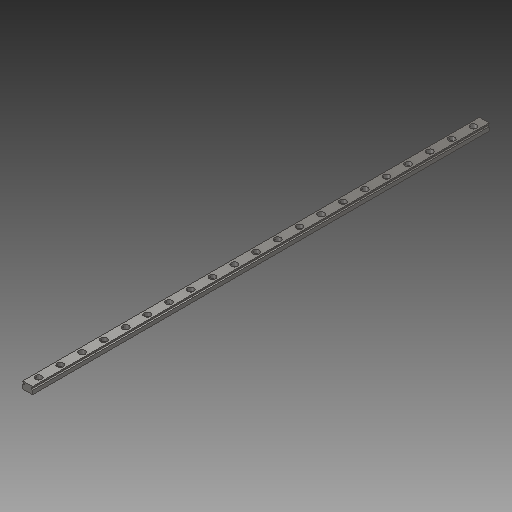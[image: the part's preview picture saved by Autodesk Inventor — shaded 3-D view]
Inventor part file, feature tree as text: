
AUTODESK INVENTOR PART (.ipt)
format: ipt  version: 2019 (Build 230136000, 136)  size: 162,304 bytes
history: native  units: mm
features: extrude x3, sketch x3, pattern_linear x2
ambient origin geometry x8: Origin, YZ Plane, XZ Plane, XY Plane, X Axis, Y Axis, Z Axis, Center Point
bodies: Solid1 (feature_tree)
feature tree (8):
  extrude  "Extrusion1"  Depth=6.5mm
  extrude  "Extrusion2"  Depth=1.0mm
  pattern_linear  "Rectangular Pattern1"  Spacing1=0.704mm  [1 undecoded]
  extrude  "Extrusion3"  Depth=420.0mm TaperAngle=0.0deg
  pattern_linear  "Rectangular Pattern2"  Spacing1=3.2mm  [1 undecoded]
  sketch  "Sketch1"  dims[d0=9.0mm d1=6.5mm]
  sketch  "Sketch2"  dims[d2=1.0mm d3=2.0mm d4=1.0mm]
  sketch  "Sketch3"  dims[d5=0.329mm d6=0.704mm d7=420.0mm d8=0.0mm d9=3.2mm d10=470.0mm d11=0.0mm d12=230.0mm d14=20.0mm d15=6.0mm d16=3.5mm d17=0.0mm d18=230.0mm d20=20.0mm]
note: 2 required parameter values undecoded (feature->parameter linkage not recoverable at this tier; creation-order binding heuristic only, values carry confidence <= 0.55)
